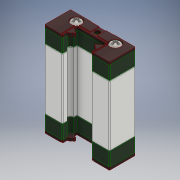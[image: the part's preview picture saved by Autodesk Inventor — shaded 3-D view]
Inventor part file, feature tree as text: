
AUTODESK INVENTOR PART (.ipt)
format: ipt  version: 2017.3 (Build 213256000, 256)  size: 475,136 bytes
history: mixed  units: mm
features: extrude x6, mirror x4, sketch x2, surface_op x1, direct_edit x1, plane x1, chamfer x1, move_body x1, imported_body x1
ambient origin geometry x8: Origin, YZ Plane, XZ Plane, XY Plane, X Axis, Y Axis, Z Axis, Center Point
bodies: Solid1 (imported_parasolid), Solid2 (imported_parasolid), Solid3 (imported_parasolid), Solid4 (imported_parasolid), Solid9 (imported_parasolid)
feature tree (18):
  surface_op  "Sculpt1"
  direct_edit  "Direct Edit1"
  plane  "Work Plane1"
  mirror  "Mirror1"
  mirror  "Mirror2"
  mirror  "Mirror3"
  extrude  "Extrusion1"  Depth=5.5mm
  mirror  "Mirror4"
  extrude  "Extrusion2"  Depth=5.0mm
  chamfer  "Chamfer1"  Distance=10.0mm
  sketch  "Sketch2"  dims[d0=0.0mm d1=5.5mm d2=0.0mm d3=5.5mm]
  sketch  "Sketch3"  dims[d4=3.8mm d5=5.0mm d6=10.0mm d7=0.0mm d8=14.45mm d10=10.0mm d11=15.0mm d12=3.0mm d13=4.0mm d14=0.0mm d15=0.4mm d16=2.0mm d17=45.0deg]
  extrude  "Extrude2"  Depth=0.4mm
  extrude  "Extrude6[1]"  Depth=10.0mm
  extrude  "Extrude6[2]"  Depth=0.4mm
  extrude  "Extrude7"  Depth=0.4mm
  move_body  "Move1"
  imported_body  NMx_Import_Brep_tag  [imported B-rep: ~327 faces, bbox_mm=[20.0, 8.0, 30.285311]]
